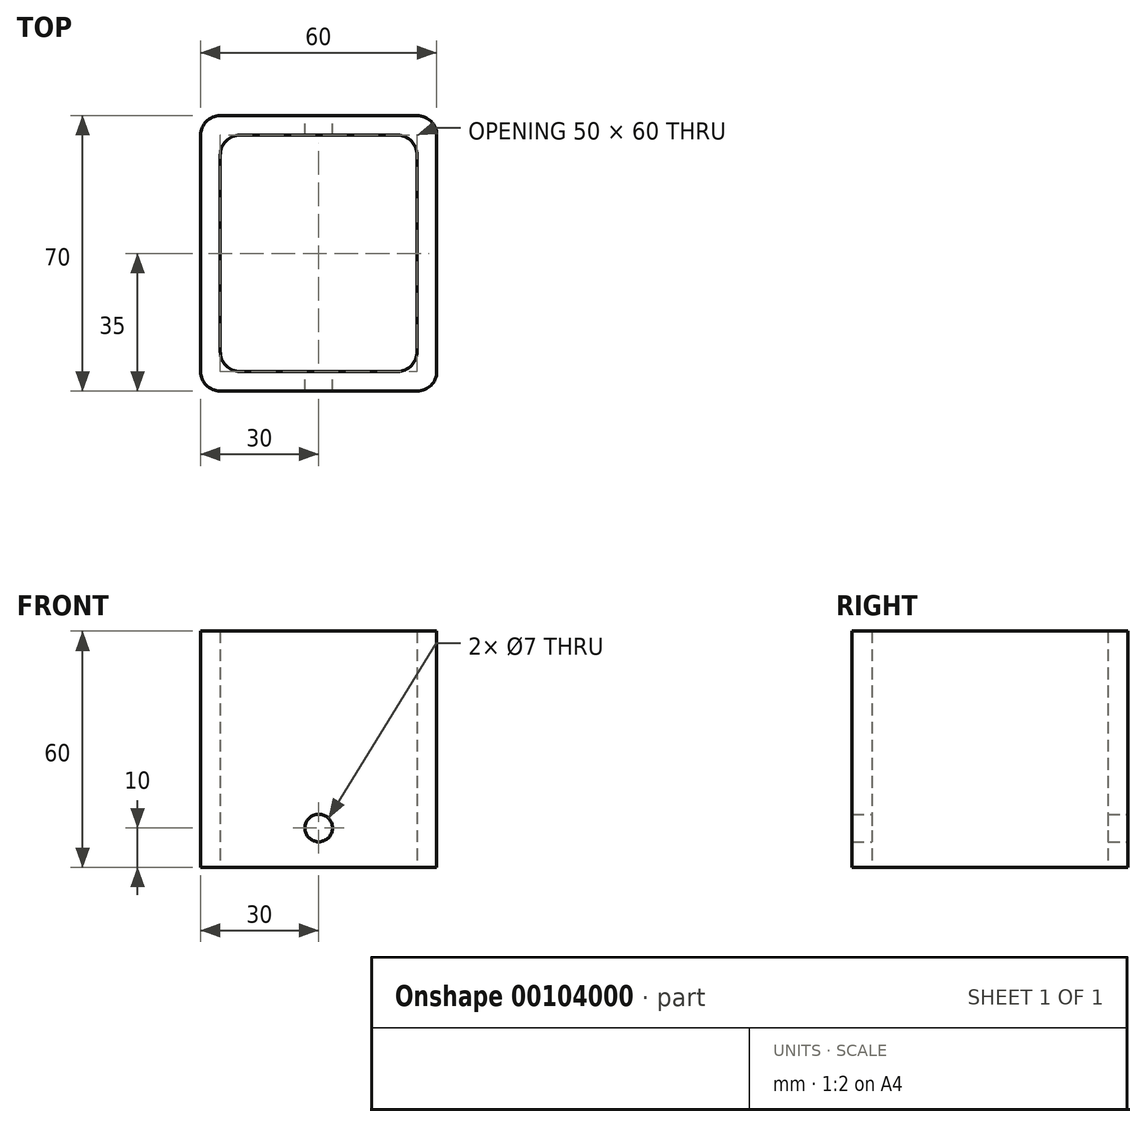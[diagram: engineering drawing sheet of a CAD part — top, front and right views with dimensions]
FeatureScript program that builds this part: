
annotation { "Feature Type Name" : "Feature", "Feature Type Description" : "" }
export const myFeature = defineFeature(function(context is Context, id is Id, definition is map)
    precondition{}
    {
        {
            var Q0;
            Q0=qCreatedBy(makeId("Top.planeOp"),FACE);
            var sketch = newSketch(context, id + "F0", { "sketchPlane" : qUnion([Q0])});
            skLineSegment(sketch, "E0.bottom", {"start": v(-25, 30) * mm, "end": v(25, 30) * mm});
            skLineSegment(sketch, "E0.top", {"start": v(-25, -30) * mm, "end": v(25, -30) * mm});
            skLineSegment(sketch, "E0.left", {"start": v(-25, 30) * mm, "end": v(-25, -30) * mm});
            skLineSegment(sketch, "E0.right", {"start": v(25, 30) * mm, "end": v(25, -30) * mm});
            skPoint(sketch, "E0.middle", {"position": v(0, 0) * mm});
            skLineSegment(sketch, "E1.bottom", {"start": v(-30, 35) * mm, "end": v(30, 35) * mm});
            skLineSegment(sketch, "E1.top", {"start": v(-30, -35) * mm, "end": v(30, -35) * mm});
            skLineSegment(sketch, "E1.left", {"start": v(-30, 35) * mm, "end": v(-30, -35) * mm});
            skLineSegment(sketch, "E1.right", {"start": v(30, 35) * mm, "end": v(30, -35) * mm});
            skSolve(sketch);
        }
        {
            var Q0;
            Q0=makeQuery(id+"F0.imprint","IMPRINT",FACE,{"disambiguationData":[TD([[makeQuery(id+"F0.imprint","IMPRINT",EDGE,{"derivedFrom":sQuery(id+"F0.wireOp",EDGE,"E0.bottom")}),1.0]])]});
            extrude(context, id + "F1", {"entities" : qUnion([Q0]), "depth" : 60 * mm});
        }
        {
            var Q0;
            Q0=makeQuery(id+"F1.opExtrude","SWEPT_EDGE",EDGE,{"disambiguationData":[OSD([sQuery(id+"F0.wireOp",EDGE,"E1.bottom"),sQuery(id+"F0.wireOp",EDGE,"E1.left")])]});
            var Q1;
            Q1=makeQuery(id+"F1.opExtrude","SWEPT_EDGE",EDGE,{"disambiguationData":[OSD([sQuery(id+"F0.wireOp",EDGE,"E1.top"),sQuery(id+"F0.wireOp",EDGE,"E1.left")])]});
            var Q2;
            Q2=makeQuery(id+"F1.opExtrude","SWEPT_EDGE",EDGE,{"disambiguationData":[OSD([sQuery(id+"F0.wireOp",EDGE,"E1.top"),sQuery(id+"F0.wireOp",EDGE,"E1.right")])]});
            var Q3;
            Q3=makeQuery(id+"F1.opExtrude","SWEPT_EDGE",EDGE,{"disambiguationData":[OSD([sQuery(id+"F0.wireOp",EDGE,"E1.bottom"),sQuery(id+"F0.wireOp",EDGE,"E1.right")])]});
            var Q4;
            Q4=makeQuery(id+"F1.opExtrude","SWEPT_EDGE",EDGE,{"disambiguationData":[OSD([sQuery(id+"F0.wireOp",EDGE,"E0.top"),sQuery(id+"F0.wireOp",EDGE,"E0.left")])]});
            var Q5;
            Q5=makeQuery(id+"F1.opExtrude","SWEPT_EDGE",EDGE,{"disambiguationData":[OSD([sQuery(id+"F0.wireOp",EDGE,"E0.top"),sQuery(id+"F0.wireOp",EDGE,"E0.right")])]});
            var Q6;
            Q6=makeQuery(id+"F1.opExtrude","SWEPT_EDGE",EDGE,{"disambiguationData":[OSD([sQuery(id+"F0.wireOp",EDGE,"E0.bottom"),sQuery(id+"F0.wireOp",EDGE,"E0.right")])]});
            var Q7;
            Q7=makeQuery(id+"F1.opExtrude","SWEPT_EDGE",EDGE,{"disambiguationData":[OSD([sQuery(id+"F0.wireOp",EDGE,"E0.bottom"),sQuery(id+"F0.wireOp",EDGE,"E0.left")])]});
            fillet(context, id + "F2", {"entities" : qUnion([Q0, Q1, Q2, Q3, Q4, Q5, Q6, Q7]), "radius" : 5 * mm, "tangentPropagation" : true, "allowEdgeOverflow" : false});
        }
        {
            var Q0;
            Q0=makeQuery(id+"F1.opExtrude","SWEPT_FACE",FACE,{"disambiguationData":[OSD([sQuery(id+"F0.wireOp",EDGE,"E1.bottom")])]});
            var sketch = newSketch(context, id + "F3", { "sketchPlane" : qUnion([Q0])});
            skCircle(sketch, "E2", {"center": v(0, 10) * mm, "radius": 3.5 * mm});
            skSolve(sketch);
        }
        {
            var Q0;
            Q0=makeQuery(id+"F3.imprint","IMPRINT",FACE,{"disambiguationData":[TD([[makeQuery(id+"F3.imprint","IMPRINT",EDGE,{"derivedFrom":sQuery(id+"F3.wireOp",EDGE,"E2")}),1.0]])]});
            extrude(context, id + "F4", {"entities" : qUnion([Q0]), "operationType" : NewBodyOperationType.REMOVE, "oppositeDirection" : true, "depth" : 70 * mm});
        }
    });
